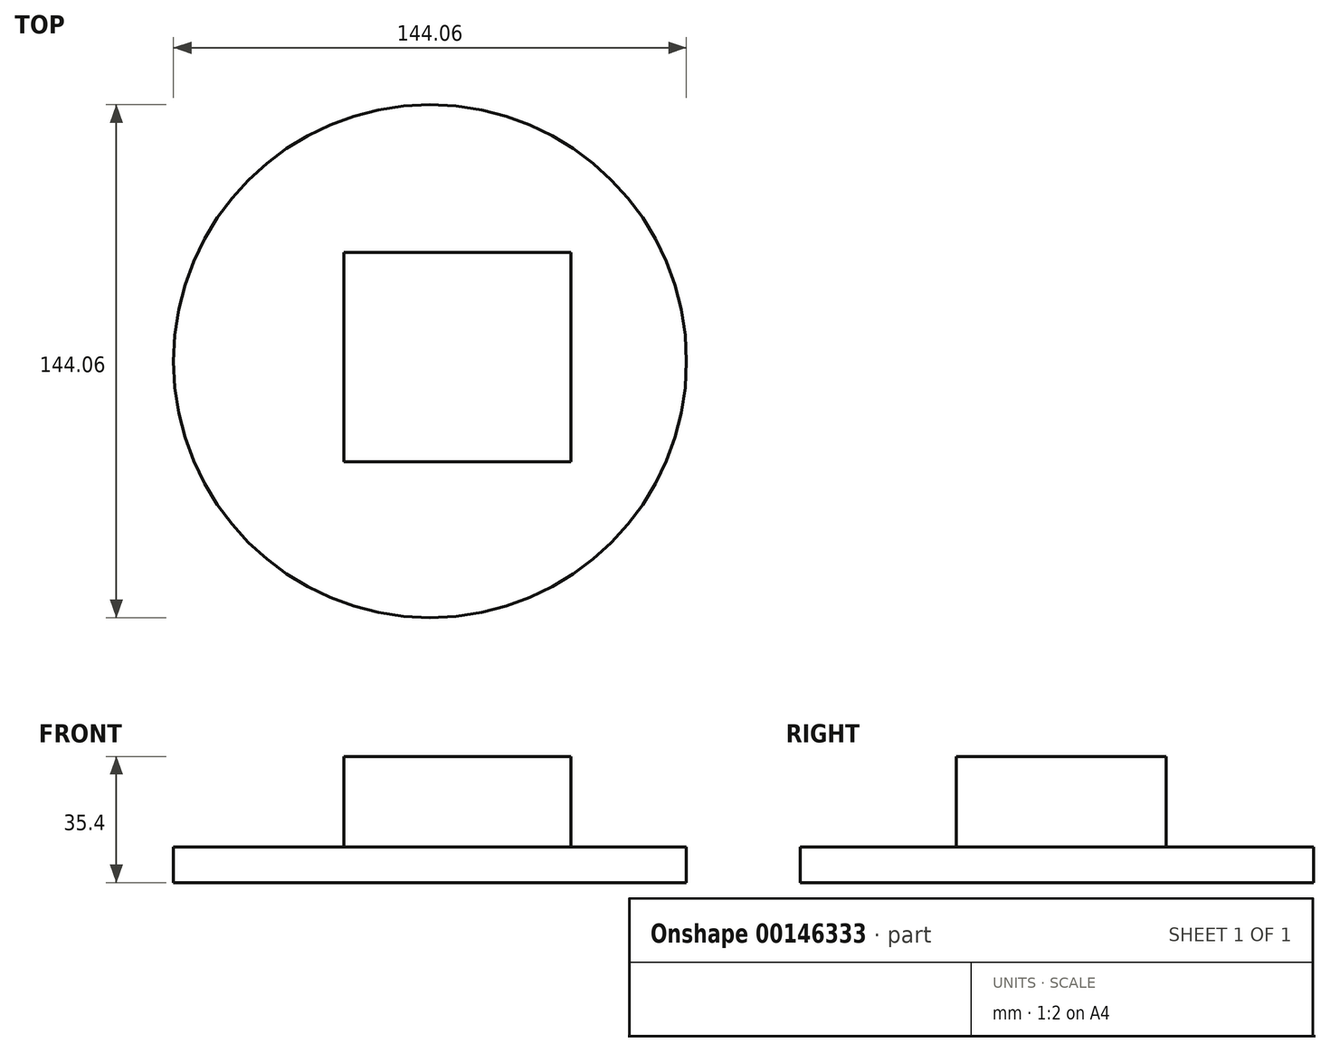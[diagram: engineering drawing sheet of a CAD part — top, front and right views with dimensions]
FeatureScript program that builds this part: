
annotation { "Feature Type Name" : "Feature", "Feature Type Description" : "" }
export const myFeature = defineFeature(function(context is Context, id is Id, definition is map)
    precondition{}
    {
        {
            var Q0;
            Q0=qCreatedBy(makeId("Top.planeOp"),FACE);
            var sketch = newSketch(context, id + "F0", { "sketchPlane" : qUnion([Q0])});
            skCircle(sketch, "E0", {"center": v(0, 0) * mm, "radius": 72.03 * mm});
            skSolve(sketch);
        }
        {
            var Q0;
            Q0 = qSketchRegion(id + "F0", true);
            extrude(context, id + "F1", {"entities" : qUnion([Q0]), "depth" : 10 * mm});
        }
        {
            var Q0;
            Q0=makeQuery(id+"F1.opExtrude","CAP_FACE",FACE,{"disambiguationData":[OSD([sQuery(id+"F0.wireOp",EDGE,"E0")])],"isStart":false});
            var sketch = newSketch(context, id + "F2", { "sketchPlane" : qUnion([Q0])});
            skLineSegment(sketch, "E1.bottom", {"start": v(-24.22, 30.62) * mm, "end": v(39.63, 30.62) * mm});
            skLineSegment(sketch, "E1.top", {"start": v(-24.22, -28.24) * mm, "end": v(39.63, -28.24) * mm});
            skLineSegment(sketch, "E1.left", {"start": v(-24.22, 30.62) * mm, "end": v(-24.22, -28.24) * mm});
            skLineSegment(sketch, "E1.right", {"start": v(39.63, 30.62) * mm, "end": v(39.63, -28.24) * mm});
            skSolve(sketch);
        }
        {
            var Q0;
            Q0 = qSketchRegion(id + "F2", true);
            extrude(context, id + "F3", {"entities" : qUnion([Q0]), "operationType" : NewBodyOperationType.ADD, "depth" : 25.4 * mm});
        }
    });
